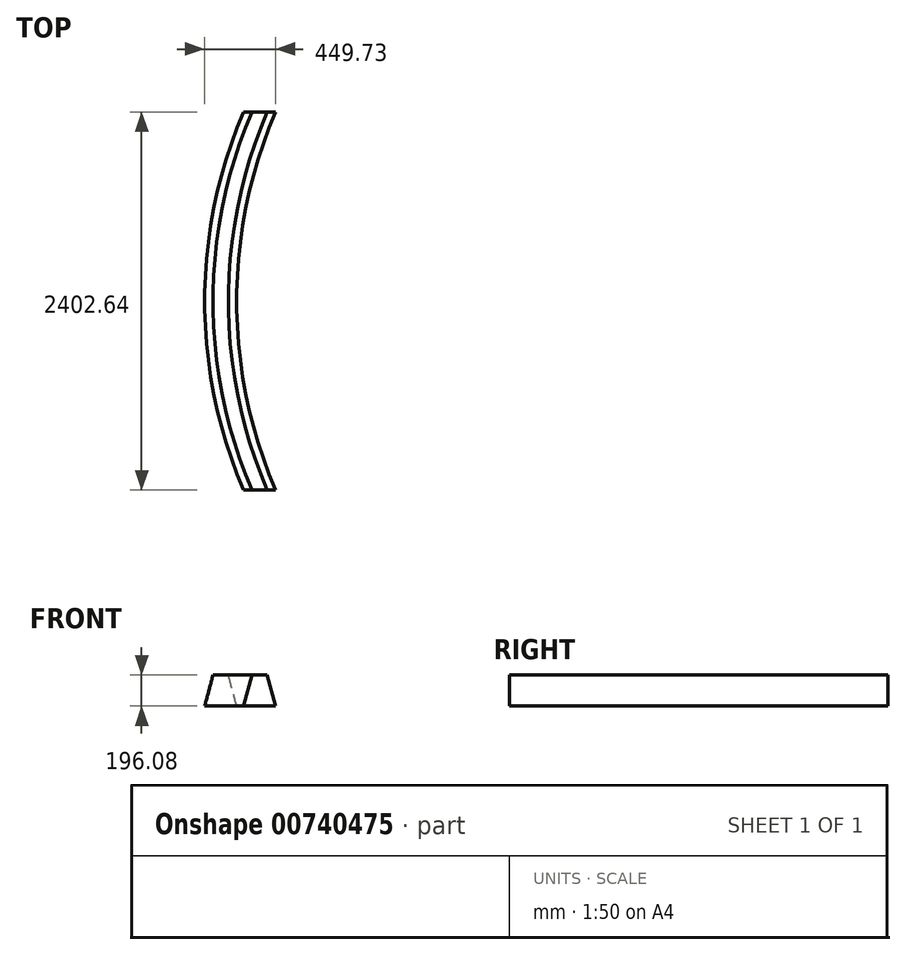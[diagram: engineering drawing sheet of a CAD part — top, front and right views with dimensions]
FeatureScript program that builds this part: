
annotation { "Feature Type Name" : "Feature", "Feature Type Description" : "" }
export const myFeature = defineFeature(function(context is Context, id is Id, definition is map)
    precondition{}
    {
        {
            var Q0;
            Q0=qCreatedBy(makeId("Front.planeOp"),FACE);
            var sketch = newSketch(context, id + "F0", { "sketchPlane" : qUnion([Q0])});
            skLineSegment(sketch, "E0", {"start": v(-101.5, -98.04) * mm, "end": v(101.5, -98.04) * mm});
            skLineSegment(sketch, "E1", {"start": v(101.5, -98.04) * mm, "end": v(48.96, 98.04) * mm});
            skLineSegment(sketch, "E2", {"start": v(48.96, 98.04) * mm, "end": v(-48.96, 98.04) * mm});
            skLineSegment(sketch, "E3", {"start": v(-48.96, 98.04) * mm, "end": v(-101.5, -98.04) * mm});
            skSolve(sketch);
        }
        {
            var Q0;
            Q0=qCreatedBy(makeId("Top.planeOp"),FACE);
            var sketch = newSketch(context, id + "F1", { "sketchPlane" : qUnion([Q0])});
            skArc(sketch, "E4", {"start": v(0, 2402.64) * mm, "mid": v(-246.73, 1201.32) * mm, "end": v(0, 0) * mm});
            skLineSegment(sketch, "E5", {"start": v(0, 0) * mm, "end": v(0, 2400) * mm, "construction": true});
            skSolve(sketch);
        }
        {
            var Q0;
            Q0=makeQuery(id+"F0.imprint","IMPRINT",FACE,{"disambiguationData":[TD([[makeQuery(id+"F0.imprint","IMPRINT",EDGE,{"derivedFrom":sQuery(id+"F0.wireOp",EDGE,"E0")}),1.0]])]});
            var Q1;
            Q1=sQuery(id+"F1.wireOp",EDGE,"E4");
            sweep(context, id + "F2", {"profiles" : qUnion([Q0]), "path" : qUnion([Q1]), "keepProfileOrientation" : true});
        }
    });
